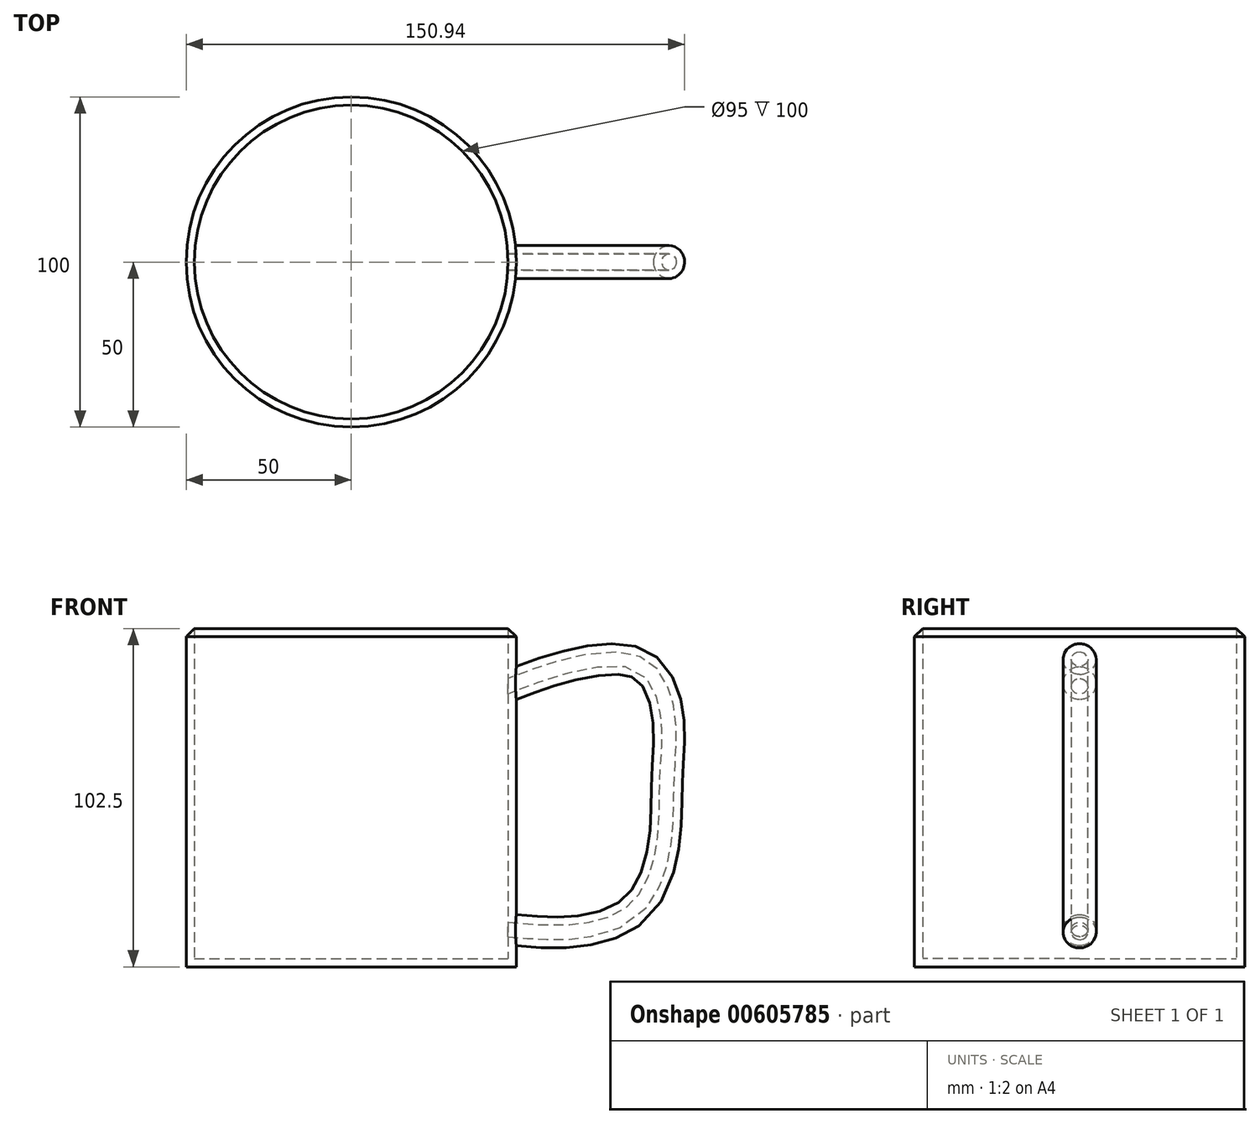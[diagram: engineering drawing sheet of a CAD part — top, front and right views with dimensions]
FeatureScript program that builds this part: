
annotation { "Feature Type Name" : "Feature", "Feature Type Description" : "" }
export const myFeature = defineFeature(function(context is Context, id is Id, definition is map)
    precondition{}
    {
        {
            var Q0;
            Q0=qCreatedBy(makeId("Top.planeOp"),FACE);
            var sketch = newSketch(context, id + "F0", { "sketchPlane" : qUnion([Q0])});
            skCircle(sketch, "E0", {"center": v(0, 0) * mm, "radius": 50 * mm});
            skSolve(sketch);
        }
        {
            var Q0;
            Q0 = qSketchRegion(id + "F0", true);
            extrude(context, id + "F1", {"entities" : qUnion([Q0]), "depth" : 105 * mm, "offsetDistance" : 25 * mm});
        }
        {
            var Q0;
            Q0=qCreatedBy(makeId("Front.planeOp"),FACE);
            var sketch = newSketch(context, id + "F2", { "sketchPlane" : qUnion([Q0])});
            skFitSpline(sketch, "E1", {"points": [v(49.65, 86.1) * mm, v(66.84, 91.74) * mm, v(88.18, 91.44) * mm, v(96.18, 75.73) * mm, v(95.89, 56.46) * mm, v(95, 37.5) * mm, v(85.8, 17.04) * mm, v(64.47, 10.23) * mm, v(46.68, 11.11) * mm, v(35.42, 13.49) * mm, v(38.98, 18.82) * mm, v(44.02, 22.97) * mm], "startDerivative": vector(164.28, 62.93) * mm, "endDerivative": vector(81.14, 62.17) * mm});
            skSolve(sketch);
        }
        {
            var Q0;
            Q0=qCreatedBy(makeId("Right.planeOp"),FACE);
            cPlane(context, id + "F3", {"entities" : qUnion([Q0]), "cplaneType" : CPlaneType.OFFSET, "offset" : 50 * mm, "width" : 150 * mm, "height" : 150 * mm});
        }
        {
            var Q0;
            Q0=qCreatedBy(id+"F3.planeOp",FACE);
            var sketch = newSketch(context, id + "F4", { "sketchPlane" : qUnion([Q0])});
            skCircle(sketch, "E2", {"center": v(0, 85.95) * mm, "radius": 5 * mm});
            skSolve(sketch);
        }
        {
            var Q0;
            Q0 = qSketchRegion(id + "F4", true);
            var Q1;
            Q1=sQuery(id+"F2.wireOp",EDGE,"E1");
            sweep(context, id + "F5", {"operationType" : NewBodyOperationType.ADD, "profiles" : qUnion([Q0]), "path" : qUnion([Q1])});
        }
        {
            var Q0;
            Q0=makeQuery(id+"F1.opExtrude","CAP_FACE",FACE,{"disambiguationData":[OSD([sQuery(id+"F0.wireOp",EDGE,"E0")])],"isStart":false});
            shell(context, id + "F6", {"entities" : qUnion([Q0]), "thickness" : 2.5 * mm});
        }
        {
            var Q0;
            Q0=makeQuery(id+"F1.opExtrude","CAP_EDGE",EDGE,{"disambiguationData":[OSD([sQuery(id+"F0.wireOp",EDGE,"E0")])],"isStart":false});
            chamfer(context, id + "F7", {"entities" : qUnion([Q0]), "width" : 5 * mm, "tangentPropagation" : true});
        }
    });
